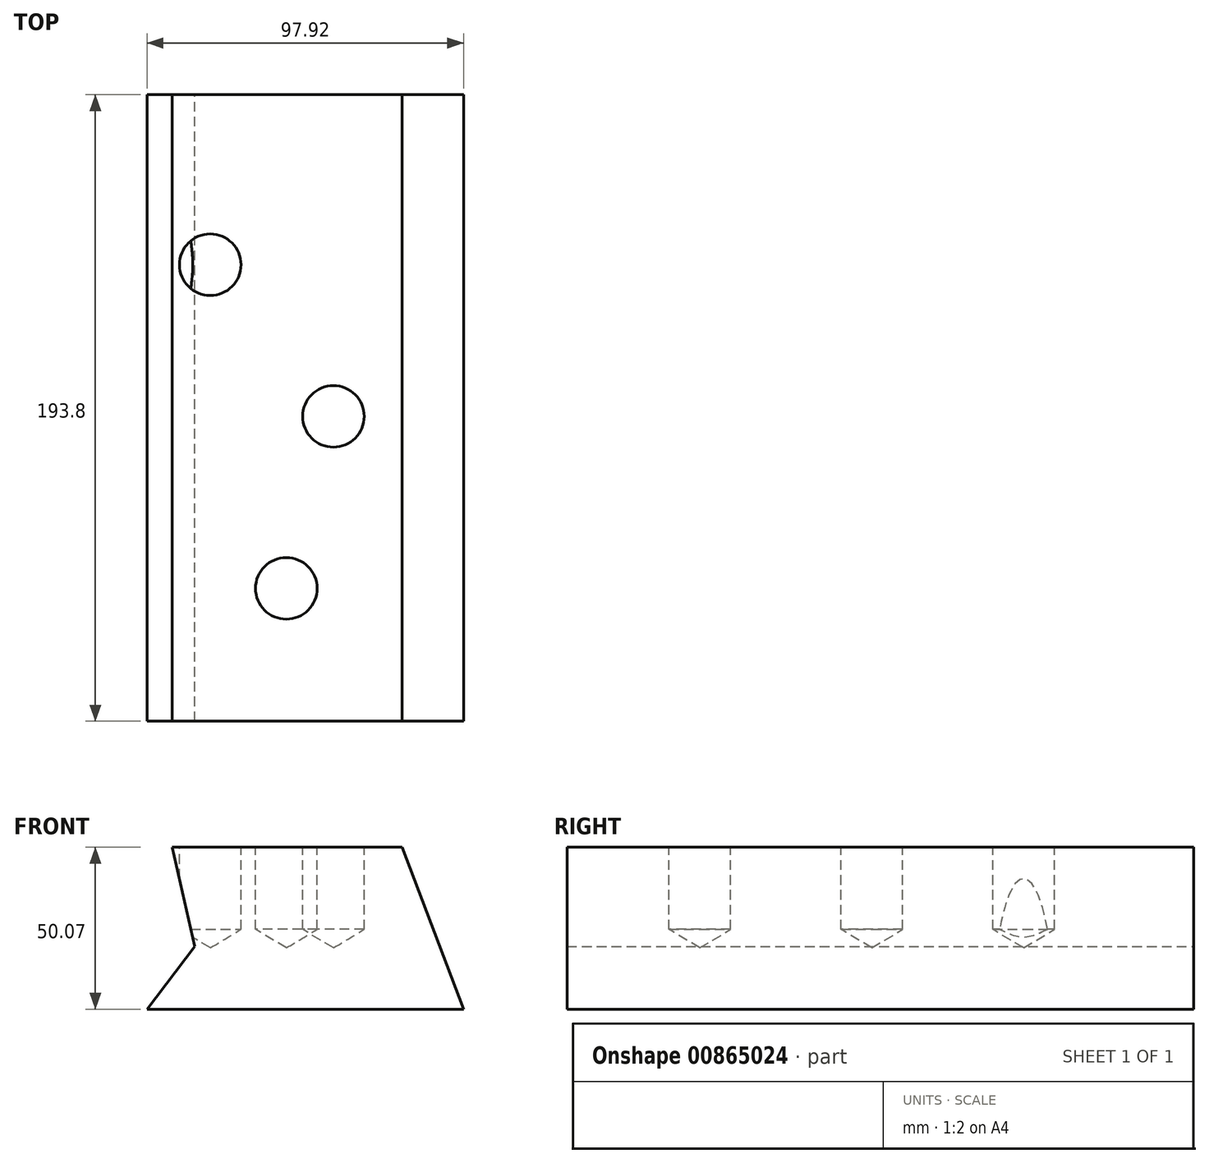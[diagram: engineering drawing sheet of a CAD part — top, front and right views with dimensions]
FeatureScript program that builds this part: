
annotation { "Feature Type Name" : "Feature", "Feature Type Description" : "" }
export const myFeature = defineFeature(function(context is Context, id is Id, definition is map)
    precondition{}
    {
        {
            var Q0;
            Q0=qCreatedBy(makeId("Front.planeOp"),FACE);
            var sketch = newSketch(context, id + "F0", { "sketchPlane" : qUnion([Q0])});
            skLineSegment(sketch, "E0", {"start": v(-43.1, 0) * mm, "end": v(54.82, 0) * mm});
            skLineSegment(sketch, "E1", {"start": v(54.82, 0) * mm, "end": v(35.85, 50.07) * mm});
            skLineSegment(sketch, "E2", {"start": v(35.85, 50.07) * mm, "end": v(-35.29, 50.07) * mm});
            skLineSegment(sketch, "E3", {"start": v(-35.29, 50.07) * mm, "end": v(-28.31, 19.39) * mm});
            skLineSegment(sketch, "E4", {"start": v(-28.31, 19.39) * mm, "end": v(-43.1, 0) * mm});
            skSolve(sketch);
        }
        {
            var Q0;
            Q0 = qSketchRegion(id + "F0", true);
            extrude(context, id + "F1", {"entities" : qUnion([Q0]), "depth" : 193.8 * mm, "offsetDistance" : 25.4 * mm});
        }
        {
            var Q0;
            Q0=makeQuery(id+"F1.opExtrude","SWEPT_FACE",FACE,{"disambiguationData":[OSD([sQuery(id+"F0.wireOp",EDGE,"E2")])]});
            var sketch = newSketch(context, id + "F2", { "sketchPlane" : qUnion([Q0])});
            skCircle(sketch, "E5", {"center": v(0, -152.7) * mm, "radius": 13.46 * mm});
            skCircle(sketch, "E6", {"center": v(14.55, -99.5) * mm, "radius": 13.16 * mm});
            skCircle(sketch, "E7", {"center": v(-23.55, -52.6) * mm, "radius": 10.29 * mm});
            skSolve(sketch);
        }
        {
            var Q0;
            Q0=sQuery(id+"F2.wireOp",VERTEX,"E5.center");
            var Q1;
            Q1=sQuery(id+"F2.wireOp",VERTEX,"E6.center");
            var Q2;
            Q2=sQuery(id+"F2.wireOp",VERTEX,"E7.center");
            var Q3;
            Q3=makeQuery(id+"F1.opExtrude","SWEPT_BODY",BODY,{"disambiguationData":[OSD([sQuery(id+"F0.wireOp",EDGE,"E0"),sQuery(id+"F0.wireOp",EDGE,"E1"),sQuery(id+"F0.wireOp",EDGE,"E2"),sQuery(id+"F0.wireOp",EDGE,"E3"),sQuery(id+"F0.wireOp",EDGE,"E4")])]});
            hole(context, id + "F3", {"style" : HoleStyle.SIMPLE, "endStyle" : HoleEndStyle.BLIND, "holeDiameter" : 19.05 * mm, "majorDiameter" : 6.35 * mm, "holeDepth" : 25.4 * mm, "isTappedThrough" : true, "tappedDepth" : 12.7 * mm, "tapClearance" : 3, "locations" : qUnion([Q0, Q1, Q2]), "scope" : qUnion([Q3])});
        }
    });
